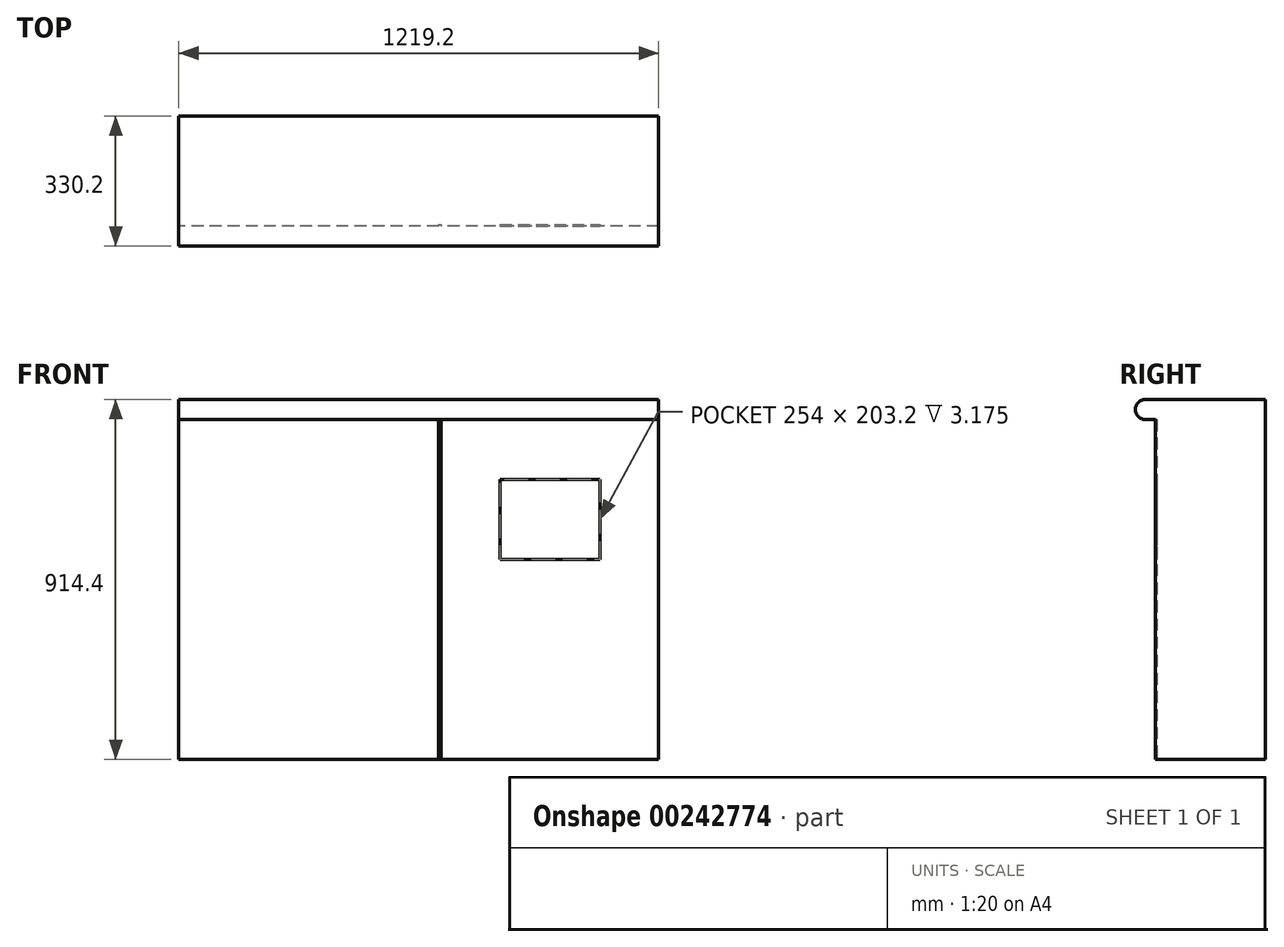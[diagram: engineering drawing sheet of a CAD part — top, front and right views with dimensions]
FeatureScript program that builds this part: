
annotation { "Feature Type Name" : "Feature", "Feature Type Description" : "" }
export const myFeature = defineFeature(function(context is Context, id is Id, definition is map)
    precondition{}
    {
        {
            var Q0;
            Q0=qCreatedBy(makeId("Top.planeOp"),FACE);
            var sketch = newSketch(context, id + "F0", { "sketchPlane" : qUnion([Q0])});
            skLineSegment(sketch, "E0.bottom", {"start": v(0, 0) * mm, "end": v(1219.2, 0) * mm});
            skLineSegment(sketch, "E0.top", {"start": v(0, -279.4) * mm, "end": v(1219.2, -279.4) * mm});
            skLineSegment(sketch, "E0.left", {"start": v(0, 0) * mm, "end": v(0, -279.4) * mm});
            skLineSegment(sketch, "E0.right", {"start": v(1219.2, 0) * mm, "end": v(1219.2, -279.4) * mm});
            skSolve(sketch);
        }
        {
            var Q0;
            Q0 = qSketchRegion(id + "F0", true);
            extrude(context, id + "F1", {"entities" : qUnion([Q0]), "depth" : 914.4 * mm});
        }
        {
            var Q0;
            Q0=makeQuery(id+"F1.opExtrude","SWEPT_FACE",FACE,{"disambiguationData":[OSD([sQuery(id+"F0.wireOp",EDGE,"E0.left")])]});
            var sketch = newSketch(context, id + "F2", { "sketchPlane" : qUnion([Q0])});
            skLineSegment(sketch, "E1", {"start": v(279.4, 914.4) * mm, "end": v(304.8, 914.4) * mm});
            skArc(sketch, "E2", {"start": v(304.8, 863.6) * mm, "mid": v(330.2, 889) * mm, "end": v(304.8, 914.4) * mm});
            skLineSegment(sketch, "E3", {"start": v(279.4, 863.6) * mm, "end": v(304.8, 863.6) * mm});
            skLineSegment(sketch, "E4", {"start": v(279.4, 914.4) * mm, "end": v(279.4, 863.6) * mm});
            skSolve(sketch);
        }
        {
            var Q0;
            Q0=makeQuery(id+"F2.imprint","IMPRINT",FACE,{"disambiguationData":[TD([[makeQuery(id+"F2.imprint","IMPRINT",EDGE,{"derivedFrom":sQuery(id+"F2.wireOp",EDGE,"E1")}),-1.0]])]});
            var Q1;
            Q1=makeQuery(id+"F1.opExtrude","SWEPT_FACE",FACE,{"disambiguationData":[OSD([sQuery(id+"F0.wireOp",EDGE,"E0.right")])]});
            extrude(context, id + "F3", {"entities" : qUnion([Q0]), "operationType" : NewBodyOperationType.ADD, "endBound" : BoundingType.UP_TO_SURFACE, "oppositeDirection" : true, "endBoundEntityFace" : qUnion([Q1]), "depth" : 25.4 * mm});
        }
        {
            var Q0;
            Q0=makeQuery(id+"F1.opExtrude","SWEPT_FACE",FACE,{"disambiguationData":[OSD([sQuery(id+"F0.wireOp",EDGE,"E0.top")])]});
            var sketch = newSketch(context, id + "F4", { "sketchPlane" : qUnion([Q0])});
            skLineSegment(sketch, "E5.bottom", {"start": v(660.4, 863.6) * mm, "end": v(666.75, 863.6) * mm});
            skLineSegment(sketch, "E5.top", {"start": v(660.4, 0) * mm, "end": v(666.75, 0) * mm});
            skLineSegment(sketch, "E5.left", {"start": v(660.4, 863.6) * mm, "end": v(660.4, 0) * mm});
            skLineSegment(sketch, "E5.right", {"start": v(666.75, 863.6) * mm, "end": v(666.75, 0) * mm});
            skLineSegment(sketch, "E6.bottom", {"start": v(815.98, 711.2) * mm, "end": v(1069.98, 711.2) * mm});
            skLineSegment(sketch, "E6.top", {"start": v(815.98, 508) * mm, "end": v(1069.98, 508) * mm});
            skLineSegment(sketch, "E6.left", {"start": v(815.98, 711.2) * mm, "end": v(815.98, 508) * mm});
            skLineSegment(sketch, "E6.right", {"start": v(1069.98, 711.2) * mm, "end": v(1069.98, 508) * mm});
            skLineSegment(sketch, "E7", {"start": v(666.75, 816.4) * mm, "end": v(1219.2, 816.4) * mm, "construction": true});
            skLineSegment(sketch, "E8", {"start": v(942.98, 816.4) * mm, "end": v(942.98, 711.2) * mm, "construction": true});
            skSolve(sketch);
        }
        {
            var Q0;
            Q0 = qSketchRegion(id + "F4", true);
            extrude(context, id + "F5", {"entities" : qUnion([Q0]), "operationType" : NewBodyOperationType.REMOVE, "oppositeDirection" : true, "depth" : 3.17 * mm});
        }
    });
